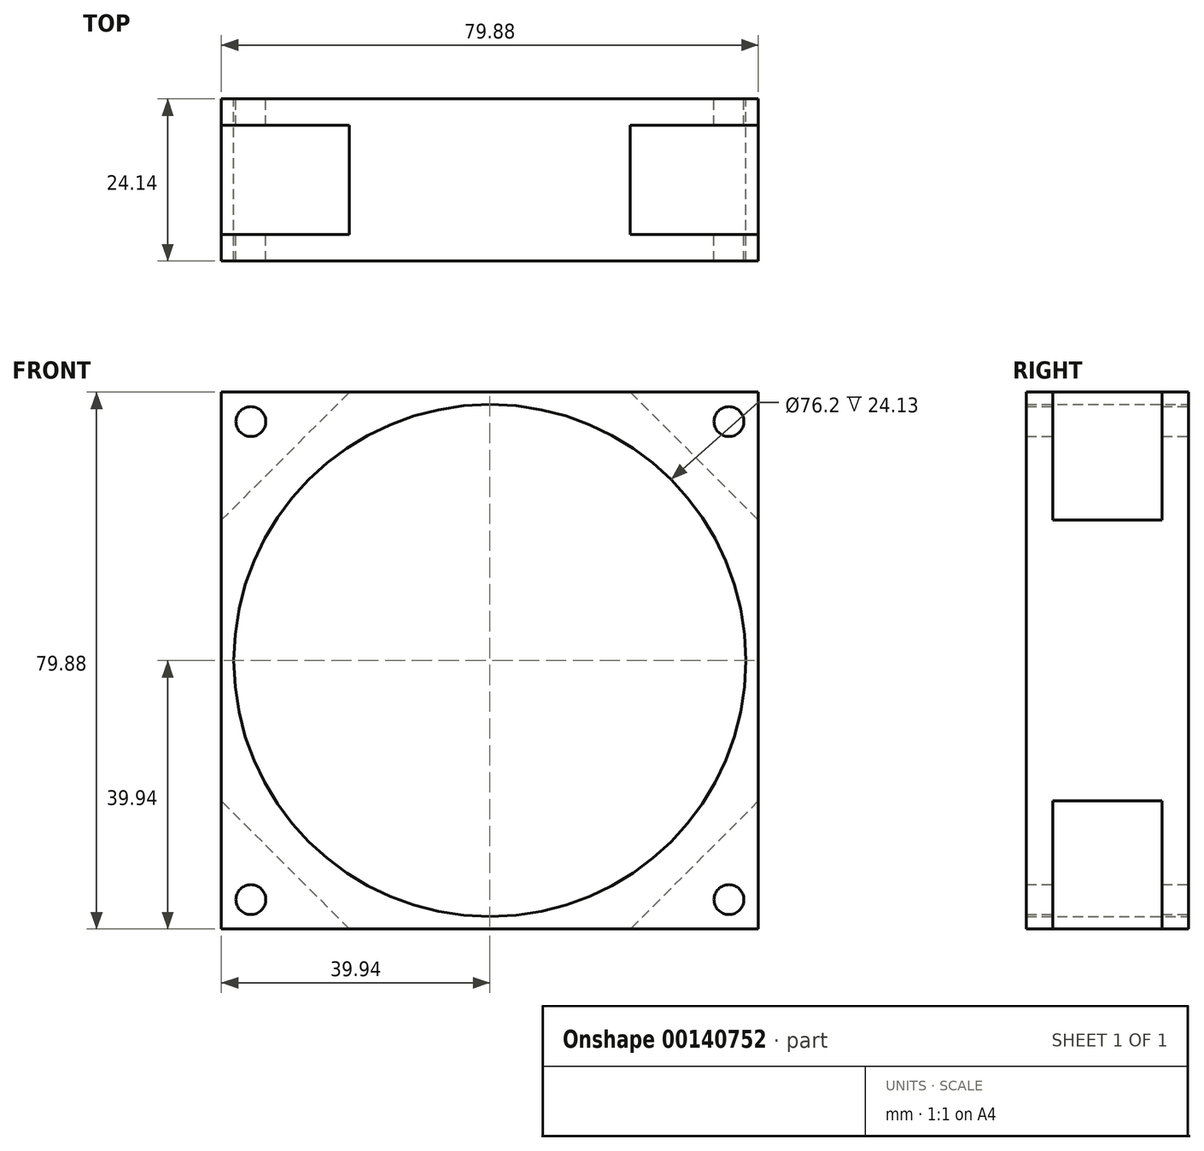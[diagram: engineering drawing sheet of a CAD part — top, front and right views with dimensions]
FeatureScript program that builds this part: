
annotation { "Feature Type Name" : "Feature", "Feature Type Description" : "" }
export const myFeature = defineFeature(function(context is Context, id is Id, definition is map)
    precondition{}
    {
        {
            var Q0;
            Q0=qCreatedBy(makeId("Front.planeOp"),FACE);
            var sketch = newSketch(context, id + "F0", { "sketchPlane" : qUnion([Q0])});
            skLineSegment(sketch, "E0.bottom", {"start": v(-39.94, 39.94) * mm, "end": v(39.94, 39.94) * mm});
            skLineSegment(sketch, "E0.top", {"start": v(-39.94, -39.94) * mm, "end": v(39.94, -39.94) * mm});
            skLineSegment(sketch, "E0.left", {"start": v(-39.94, 39.94) * mm, "end": v(-39.94, -39.94) * mm});
            skLineSegment(sketch, "E0.right", {"start": v(39.94, 39.94) * mm, "end": v(39.94, -39.94) * mm});
            skPoint(sketch, "E0.middle", {"position": v(0, 0) * mm});
            skCircle(sketch, "E1", {"center": v(-35.56, 35.56) * mm, "radius": 2.22 * mm});
            skCircle(sketch, "E2", {"center": v(-35.56, -35.56) * mm, "radius": 2.22 * mm});
            skCircle(sketch, "E3", {"center": v(35.56, -35.56) * mm, "radius": 2.22 * mm});
            skCircle(sketch, "E4", {"center": v(35.56, 35.56) * mm, "radius": 2.22 * mm});
            skCircle(sketch, "E5", {"center": v(0, 0) * mm, "radius": 38.1 * mm});
            skLineSegment(sketch, "E6", {"start": v(-39.94, 20.9) * mm, "end": v(-20.9, 39.94) * mm});
            skLineSegment(sketch, "E7", {"start": v(20.9, 39.94) * mm, "end": v(39.94, 20.9) * mm});
            skLineSegment(sketch, "E8", {"start": v(39.94, -20.9) * mm, "end": v(20.9, -39.94) * mm});
            skLineSegment(sketch, "E9", {"start": v(-20.9, -39.94) * mm, "end": v(-39.94, -20.9) * mm});
            skSolve(sketch);
        }
        {
            var Q0;
            Q0=makeQuery(id+"F0.imprint","IMPRINT",FACE,{"disambiguationData":[TD([[makeQuery(id+"F0.imprint","IMPRINT",EDGE,{"derivedFrom":sQuery(id+"F0.wireOp",EDGE,"E1")}),-1.0]])]});
            var Q1;
            Q1=makeQuery(id+"F0.imprint","IMPRINT",FACE,{"disambiguationData":[TD([[makeQuery(id+"F0.imprint","IMPRINT",EDGE,{"derivedFrom":sQuery(id+"F0.wireOp",EDGE,"E5")}),-1.0]])]});
            var Q2;
            Q2=makeQuery(id+"F0.imprint","IMPRINT",FACE,{"disambiguationData":[TD([[makeQuery(id+"F0.imprint","IMPRINT",EDGE,{"derivedFrom":sQuery(id+"F0.wireOp",EDGE,"E4")}),-1.0]])]});
            var Q3;
            Q3=makeQuery(id+"F0.imprint","IMPRINT",FACE,{"disambiguationData":[TD([[makeQuery(id+"F0.imprint","IMPRINT",EDGE,{"derivedFrom":sQuery(id+"F0.wireOp",EDGE,"E3")}),-1.0]])]});
            var Q4;
            Q4=makeQuery(id+"F0.imprint","IMPRINT",FACE,{"disambiguationData":[TD([[makeQuery(id+"F0.imprint","IMPRINT",EDGE,{"derivedFrom":sQuery(id+"F0.wireOp",EDGE,"E2")}),-1.0]])]});
            extrude(context, id + "F1", {"entities" : qUnion([Q0, Q1, Q2, Q3, Q4]), "endBound" : BoundingType.SYMMETRIC, "depth" : 24.13 * mm});
        }
        {
            var Q0;
            Q0=makeQuery(id+"F0.imprint","IMPRINT",FACE,{"disambiguationData":[TD([[makeQuery(id+"F0.imprint","IMPRINT",EDGE,{"derivedFrom":sQuery(id+"F0.wireOp",EDGE,"E1")}),-1.0]])]});
            var Q1;
            Q1=makeQuery(id+"F0.imprint","IMPRINT",FACE,{"disambiguationData":[TD([[makeQuery(id+"F0.imprint","IMPRINT",EDGE,{"derivedFrom":sQuery(id+"F0.wireOp",EDGE,"E4")}),-1.0]])]});
            var Q2;
            Q2=makeQuery(id+"F0.imprint","IMPRINT",FACE,{"disambiguationData":[TD([[makeQuery(id+"F0.imprint","IMPRINT",EDGE,{"derivedFrom":sQuery(id+"F0.wireOp",EDGE,"E3")}),-1.0]])]});
            var Q3;
            Q3=makeQuery(id+"F0.imprint","IMPRINT",FACE,{"disambiguationData":[TD([[makeQuery(id+"F0.imprint","IMPRINT",EDGE,{"derivedFrom":sQuery(id+"F0.wireOp",EDGE,"E2")}),-1.0]])]});
            extrude(context, id + "F2", {"entities" : qUnion([Q0, Q1, Q2, Q3]), "operationType" : NewBodyOperationType.REMOVE, "endBound" : BoundingType.SYMMETRIC, "oppositeDirection" : true, "depth" : 16.26 * mm});
        }
    });
